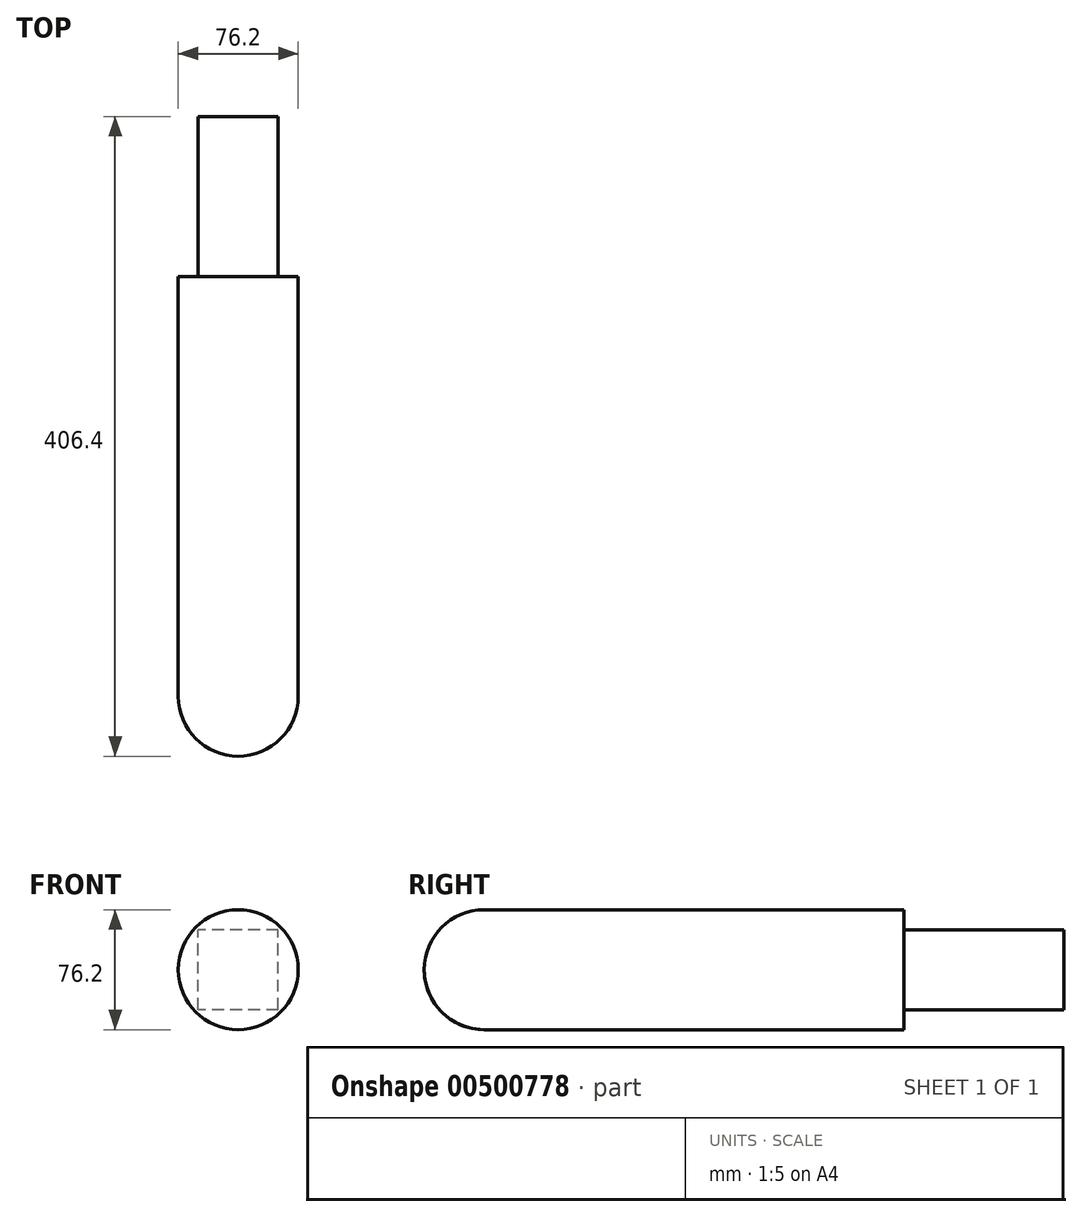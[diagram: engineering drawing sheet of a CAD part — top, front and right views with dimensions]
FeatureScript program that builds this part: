
annotation { "Feature Type Name" : "Feature", "Feature Type Description" : "" }
export const myFeature = defineFeature(function(context is Context, id is Id, definition is map)
    precondition{}
    {
        {
            var Q0;
            Q0=qCreatedBy(makeId("Front.planeOp"),FACE);
            var sketch = newSketch(context, id + "F0", { "sketchPlane" : qUnion([Q0])});
            skLineSegment(sketch, "E0.bottom", {"start": v(25.4, -25.4) * mm, "end": v(-25.4, -25.4) * mm});
            skLineSegment(sketch, "E0.top", {"start": v(25.4, 25.4) * mm, "end": v(-25.4, 25.4) * mm});
            skLineSegment(sketch, "E0.left", {"start": v(25.4, -25.4) * mm, "end": v(25.4, 25.4) * mm});
            skLineSegment(sketch, "E0.right", {"start": v(-25.4, -25.4) * mm, "end": v(-25.4, 25.4) * mm});
            skPoint(sketch, "E0.middle", {"position": v(0, 0) * mm});
            skSolve(sketch);
        }
        {
            var Q0;
            Q0=makeQuery(id+"F0.imprint","IMPRINT",FACE,{"disambiguationData":[TD([[makeQuery(id+"F0.imprint","IMPRINT",EDGE,{"derivedFrom":sQuery(id+"F0.wireOp",EDGE,"E0.bottom")}),-1.0]])]});
            extrude(context, id + "F1", {"entities" : qUnion([Q0]), "depth" : 101.6 * mm});
        }
        {
            var Q0;
            Q0=makeQuery(id+"F1.opExtrude","CAP_FACE",FACE,{"disambiguationData":[OSD([sQuery(id+"F0.wireOp",EDGE,"E0.bottom"),sQuery(id+"F0.wireOp",EDGE,"E0.top"),sQuery(id+"F0.wireOp",EDGE,"E0.left"),sQuery(id+"F0.wireOp",EDGE,"E0.right")])],"isStart":false});
            var sketch = newSketch(context, id + "F2", { "sketchPlane" : qUnion([Q0])});
            skCircle(sketch, "E1", {"center": v(0, 0) * mm, "radius": 38.1 * mm});
            skSolve(sketch);
        }
        {
            var Q0;
            Q0=makeQuery(id+"F2.imprint","IMPRINT",FACE,{"disambiguationData":[TD([[makeQuery(id+"F2.imprint","IMPRINT",EDGE,{"derivedFrom":sQuery(id+"F2.wireOp",EDGE,"E1")}),1.0]])]});
            var Q1;
            Q1=makeQuery(id+"F2.imprint","IMPRINT",FACE,{"disambiguationData":[TD([[makeQuery(id+"F2.imprint","IMPRINT",EDGE,{"derivedFrom":makeQuery(id+"F1.opExtrude","CAP_EDGE",EDGE,{"disambiguationData":[OSD([sQuery(id+"F0.wireOp",EDGE,"E0.bottom")])],"isStart":false})}),-1.0]])]});
            extrude(context, id + "F3", {"entities" : qUnion([Q0, Q1]), "operationType" : NewBodyOperationType.ADD, "depth" : 304.8 * mm});
        }
        {
            var Q0;
            Q0=makeQuery(id+"F3.opExtrude","CAP_EDGE",EDGE,{"disambiguationData":[OSD([sQuery(id+"F2.wireOp",EDGE,"E1")])],"isStart":false});
            fillet(context, id + "F4", {"entities" : qUnion([Q0]), "radius" : 38.1 * mm, "tangentPropagation" : true, "allowEdgeOverflow" : false});
        }
    });
